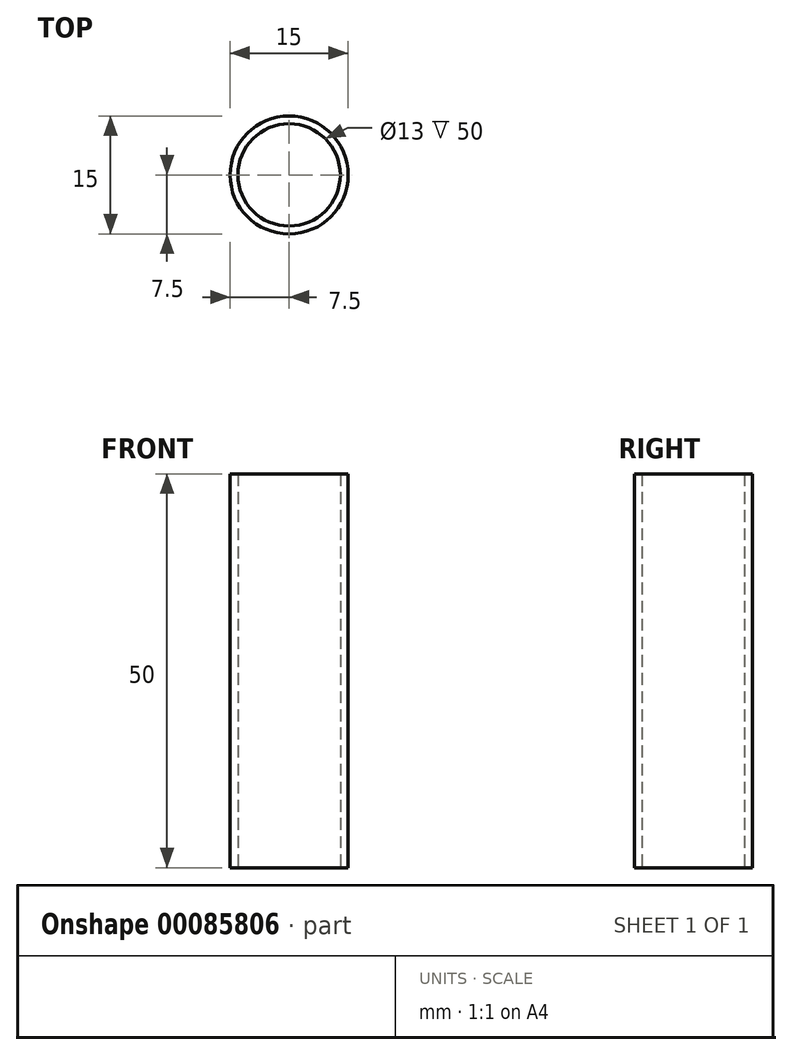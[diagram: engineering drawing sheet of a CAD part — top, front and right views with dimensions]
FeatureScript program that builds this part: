
annotation { "Feature Type Name" : "Feature", "Feature Type Description" : "" }
export const myFeature = defineFeature(function(context is Context, id is Id, definition is map)
    precondition{}
    {
        {
            var Q0;
            Q0=qCreatedBy(makeId("Top.planeOp"),FACE);
            var sketch = newSketch(context, id + "F0", { "sketchPlane" : qUnion([Q0])});
            skCircle(sketch, "E0", {"center": v(0, 0) * mm, "radius": 7.5 * mm});
            skCircle(sketch, "E1", {"center": v(0, 0) * mm, "radius": 6.5 * mm});
            skSolve(sketch);
        }
        {
            var Q0;
            Q0=makeQuery(id+"F0.imprint","IMPRINT",FACE,{"disambiguationData":[TD([[makeQuery(id+"F0.imprint","IMPRINT",EDGE,{"derivedFrom":sQuery(id+"F0.wireOp",EDGE,"E0")}),1.0]])]});
            extrude(context, id + "F1", {"entities" : qUnion([Q0]), "depth" : 50 * mm});
        }
    });
